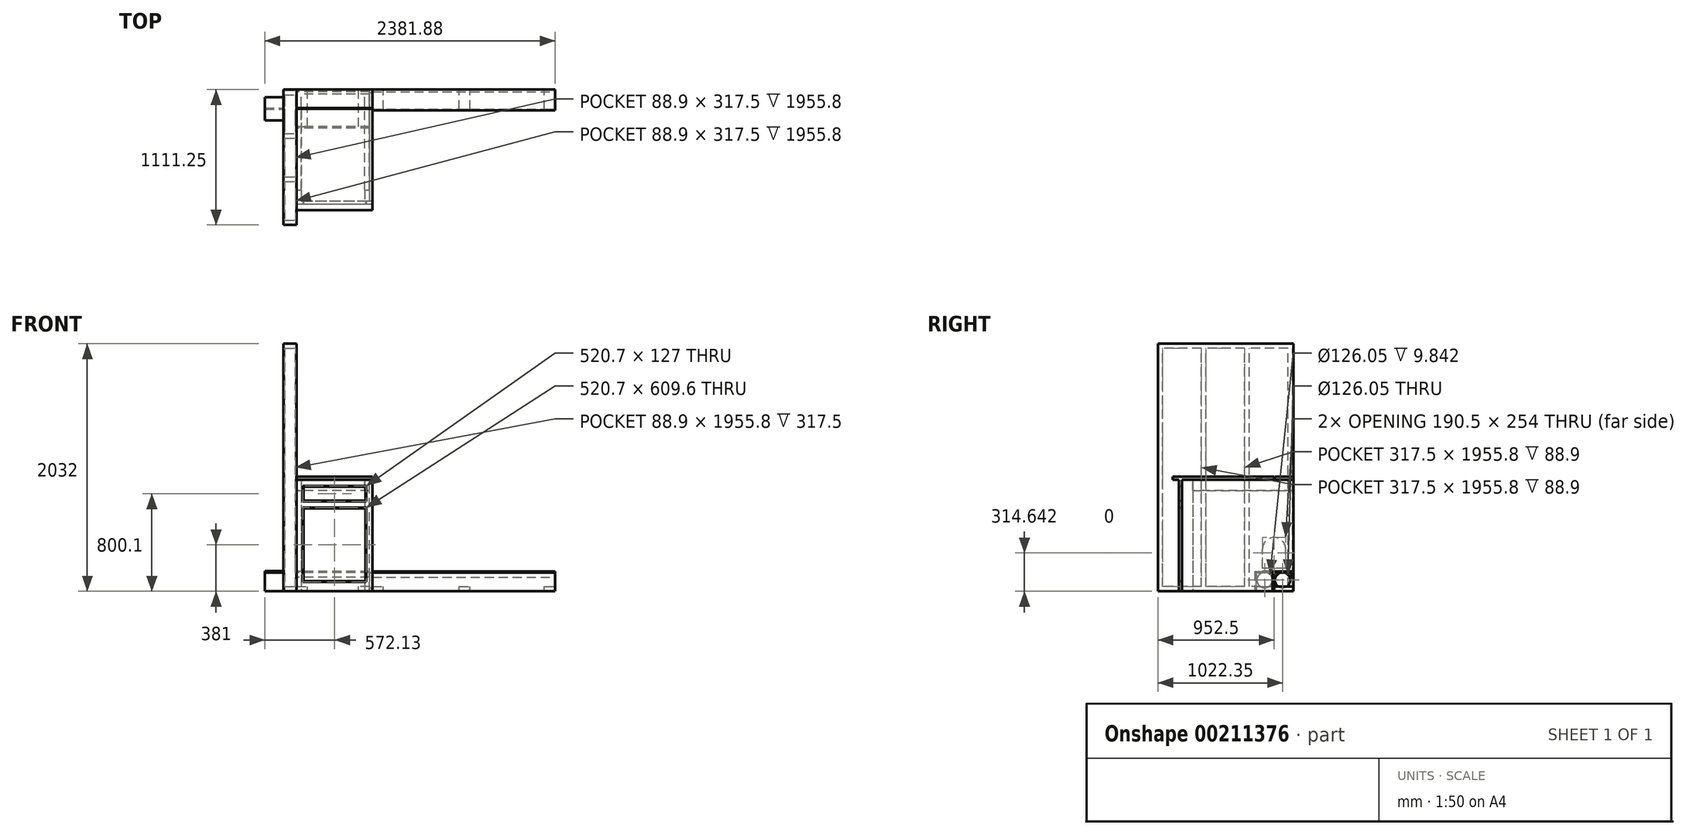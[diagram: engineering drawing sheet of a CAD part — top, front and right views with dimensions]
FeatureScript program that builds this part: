
annotation { "Feature Type Name" : "Feature", "Feature Type Description" : "" }
export const myFeature = defineFeature(function(context is Context, id is Id, definition is map)
    precondition{}
    {
        {
            var Q0;
            Q0=qCreatedBy(makeId("Right.planeOp"),FACE);
            cPlane(context, id + "F0", {"entities" : qUnion([Q0]), "cplaneType" : CPlaneType.OFFSET, "offset" : 1060.45 * mm, "width" : 152.4 * mm, "height" : 152.4 * mm});
        }
        {
            var Q0;
            Q0=qCreatedBy(makeId("Right.planeOp"),FACE);
            cPlane(context, id + "F1", {"entities" : qUnion([Q0]), "cplaneType" : CPlaneType.OFFSET, "offset" : 1060.45 * mm, "oppositeDirection" : true, "width" : 152.4 * mm, "height" : 152.4 * mm});
        }
        {
            var Q0;
            Q0=qCreatedBy(makeId("Top.planeOp"),FACE);
            cPlane(context, id + "F2", {"entities" : qUnion([Q0]), "cplaneType" : CPlaneType.OFFSET, "offset" : 914.4 * mm, "oppositeDirection" : true, "width" : 152.4 * mm, "height" : 152.4 * mm});
        }
        {
            var Q0;
            Q0=qCreatedBy(id+"F2.planeOp",FACE);
            cPlane(context, id + "F3", {"entities" : qUnion([Q0]), "cplaneType" : CPlaneType.OFFSET, "offset" : 2032 * mm, "width" : 152.4 * mm, "height" : 152.4 * mm});
        }
        {
            var Q0;
            Q0=qCreatedBy(makeId("Front.planeOp"),FACE);
            cPlane(context, id + "F4", {"entities" : qUnion([Q0]), "cplaneType" : CPlaneType.OFFSET, "offset" : 914.4 * mm, "oppositeDirection" : true, "width" : 152.4 * mm, "height" : 152.4 * mm});
        }
        {
            var Q0;
            Q0=qCreatedBy(id+"F4.planeOp",FACE);
            cPlane(context, id + "F5", {"entities" : qUnion([Q0]), "cplaneType" : CPlaneType.OFFSET, "offset" : 1111.25 * mm, "width" : 152.4 * mm, "height" : 152.4 * mm});
        }
        {
            var Q0;
            Q0=qCreatedBy(id+"F2.planeOp",FACE);
            var sketch = newSketch(context, id + "F6", { "sketchPlane" : qUnion([Q0])});
            skLineSegment(sketch, "E0.bottom", {"start": v(-1060.45, 914.4) * mm, "end": v(1060.45, 914.4) * mm});
            skLineSegment(sketch, "E0.top", {"start": v(-1060.45, -196.85) * mm, "end": v(1060.45, -196.85) * mm});
            skLineSegment(sketch, "E0.left", {"start": v(-1060.45, 914.4) * mm, "end": v(-1060.45, -196.85) * mm});
            skLineSegment(sketch, "E0.right", {"start": v(1060.45, 914.4) * mm, "end": v(1060.45, -196.85) * mm});
            skSolve(sketch);
        }
        {
            var Q0;
            Q0=qCreatedBy(id+"F2.planeOp",FACE);
            var sketch = newSketch(context, id + "F7", { "sketchPlane" : qUnion([Q0])});
            skLineSegment(sketch, "E1", {"start": v(-1060.45, 0) * mm, "end": v(1060.45, 0) * mm, "construction": true});
            skSolve(sketch);
        }
        {
            var Q0;
            Q0=qCreatedBy(id+"F2.planeOp",FACE);
            var sketch = newSketch(context, id + "F8", { "sketchPlane" : qUnion([Q0])});
            skLineSegment(sketch, "E2", {"start": v(-450.85, 914.4) * mm, "end": v(-450.85, 0) * mm, "construction": true});
            skSolve(sketch);
        }
        {
            var Q0;
            Q0 = qBodyType(qCreatedBy(id + "F8" ,EDGE), BodyType.WIRE);
            var Q1;
            Q1=qCreatedBy(id+"F1.planeOp",FACE);
            cPlane(context, id + "F9", {"entities" : qUnion([Q0, Q1]), "cplaneType" : CPlaneType.LINE_ANGLE, "offset" : 25.4 * mm, "angle" : 0 * degree, "width" : 152.4 * mm, "height" : 152.4 * mm});
        }
        {
            var Q0;
            Q0=qCreatedBy(id+"F2.planeOp",FACE);
            var sketch = newSketch(context, id + "F10", { "sketchPlane" : qUnion([Q0])});
            skPoint(sketch, "E3", {"position": v(1060.45, 825.5) * mm});
            skPoint(sketch, "E4", {"position": v(-1060.45, 679.45) * mm});
            skPoint(sketch, "E5", {"position": v(-1060.45, 342.9) * mm});
            skSolve(sketch);
        }
        {
            var Q0;
            Q0=qCreatedBy(id+"F1.planeOp",FACE);
            var sketch = newSketch(context, id + "F11", { "sketchPlane" : qUnion([Q0])});
            skCircle(sketch, "E6", {"center": v(678.37, -822.33) * mm, "radius": 53.18 * mm});
            skSolve(sketch);
        }
        {
            var Q0;
            Q0=qCreatedBy(id+"F0.planeOp",FACE);
            var sketch = newSketch(context, id + "F12", { "sketchPlane" : qUnion([Q0])});
            skCircle(sketch, "E7", {"center": v(825.5, -822.33) * mm, "radius": 53.18 * mm});
            skSolve(sketch);
        }
        {
            var Q0;
            Q0=makeQuery(id+"F6.imprint","IMPRINT",FACE,{"disambiguationData":[TD([[makeQuery(id+"F6.imprint","IMPRINT",EDGE,{"derivedFrom":sQuery(id+"F6.wireOp",EDGE,"E0.bottom")}),-1.0]])]});
            cPlane(context, id + "F13", {"entities" : qUnion([Q0]), "cplaneType" : CPlaneType.OFFSET, "offset" : 92.07 * mm, "width" : 152.4 * mm, "height" : 152.4 * mm});
        }
        {
            var Q0;
            Q0=qCreatedBy(id+"F13.planeOp",FACE);
            var sketch = newSketch(context, id + "F14", { "sketchPlane" : qUnion([Q0])});
            skLineSegment(sketch, "E8", {"start": v(-1060.45, 678.37) * mm, "end": v(-908.05, 678.37) * mm});
            skLineSegment(sketch, "E9", {"start": v(-908.05, 678.37) * mm, "end": v(-760.92, 825.5) * mm});
            skLineSegment(sketch, "E10", {"start": v(-760.92, 825.5) * mm, "end": v(1060.45, 825.5) * mm});
            skSolve(sketch);
        }
        {
            var Q0;
            Q0 = qSketchRegion(id + "F12", true);
            var Q1;
            Q1=sQuery(id+"F11.wireOp",EDGE,"E6");
            var Q2;
            Q2 = qConstructionFilter(qBodyType(qCreatedBy(id + "F14" ,EDGE), BodyType.WIRE), ConstructionObject.NO);
            sweep(context, id + "F15", {"bodyType" : ToolBodyType.SURFACE, "profiles" : qUnion([Q0]), "surfaceProfiles" : qUnion([Q1]), "path" : qUnion([Q2])});
        }
        {
            var Q0;
            Q0=qCreatedBy(id+"F2.planeOp",FACE);
            var sketch = newSketch(context, id + "F16", { "sketchPlane" : qUnion([Q0])});
            skLineSegment(sketch, "E11", {"start": v(-1060.45, 596.9) * mm, "end": v(1060.45, 596.9) * mm, "construction": true});
            skSolve(sketch);
        }
        {
            var Q0;
            Q0=makeQuery(id+"F6.imprint","IMPRINT",FACE,{"disambiguationData":[TD([[makeQuery(id+"F6.imprint","IMPRINT",EDGE,{"derivedFrom":sQuery(id+"F6.wireOp",EDGE,"E0.bottom")}),-1.0]])]});
            var sketch = newSketch(context, id + "F17", { "sketchPlane" : qUnion([Q0])});
            skPoint(sketch, "E12", {"position": v(1060.45, 742.95) * mm});
            skLineSegment(sketch, "E13", {"start": v(1060.45, 742.95) * mm, "end": v(-1060.45, 742.95) * mm, "construction": true});
            skSolve(sketch);
        }
        {
            var Q0;
            Q0=qCreatedBy(id+"F1.planeOp",FACE);
            var sketch = newSketch(context, id + "F18", { "sketchPlane" : qUnion([Q0])});
            skLineSegment(sketch, "E14.bottom", {"start": v(914.4, -762) * mm, "end": v(596.9, -762) * mm});
            skLineSegment(sketch, "E14.top", {"start": v(914.4, -752.16) * mm, "end": v(596.9, -752.16) * mm});
            skLineSegment(sketch, "E14.left", {"start": v(914.4, -762) * mm, "end": v(914.4, -752.16) * mm});
            skLineSegment(sketch, "E14.right", {"start": v(596.9, -762) * mm, "end": v(596.9, -752.16) * mm});
            skPoint(sketch, "E15.0", {"position": v(914.4, -914.4) * mm});
            skPoint(sketch, "E16.0", {"position": v(596.9, -914.4) * mm});
            skSolve(sketch);
        }
        {
            var Q0;
            Q0=qCreatedBy(id+"F0.planeOp",FACE);
            var sketch = newSketch(context, id + "F19", { "sketchPlane" : qUnion([Q0])});
            skLineSegment(sketch, "E17.bottom", {"start": v(914.4, -752.16) * mm, "end": v(742.95, -752.16) * mm});
            skLineSegment(sketch, "E17.top", {"start": v(914.4, -762) * mm, "end": v(742.95, -762) * mm});
            skLineSegment(sketch, "E17.left", {"start": v(914.4, -752.16) * mm, "end": v(914.4, -762) * mm});
            skLineSegment(sketch, "E17.right", {"start": v(742.95, -752.16) * mm, "end": v(742.95, -762) * mm});
            skSolve(sketch);
        }
        {
            var Q0;
            Q0=qCreatedBy(id+"F9.planeOp",FACE);
            var sketch = newSketch(context, id + "F20", { "sketchPlane" : qUnion([Q0])});
            skLineSegment(sketch, "E18.bottom", {"start": v(-914.4, -914.4) * mm, "end": v(0, -914.4) * mm});
            skLineSegment(sketch, "E18.top", {"start": v(-914.4, 0) * mm, "end": v(0, 0) * mm});
            skLineSegment(sketch, "E18.left", {"start": v(-914.4, -914.4) * mm, "end": v(-914.4, 0) * mm});
            skLineSegment(sketch, "E18.right", {"start": v(0, -914.4) * mm, "end": v(0, 0) * mm});
            skCircle(sketch, "E19", {"center": v(-825.5, -822.33) * mm, "radius": 63.02 * mm});
            skSolve(sketch);
        }
        {
            var Q0;
            Q0 = qSketchRegion(id + "F20", true);
            extrude(context, id + "F21", {"entities" : qUnion([Q0]), "endBound" : BoundingType.SYMMETRIC, "depth" : 25.4 * mm});
        }
        {
            var Q0;
            Q0=makeQuery(id+"F18.imprint","IMPRINT",FACE,{"disambiguationData":[TD([[makeQuery(id+"F18.imprint","IMPRINT",EDGE,{"derivedFrom":sQuery(id+"F18.wireOp",EDGE,"E14.bottom")}),-1.0]])]});
            var Q1;
            Q1=makeQuery(id+"F21.opExtrude","CAP_FACE",FACE,{"disambiguationData":[OSD([sQuery(id+"F20.wireOp",EDGE,"E18.bottom"),sQuery(id+"F20.wireOp",EDGE,"E18.top"),sQuery(id+"F20.wireOp",EDGE,"E18.left"),sQuery(id+"F20.wireOp",EDGE,"E18.right"),sQuery(id+"F20.wireOp",EDGE,"E19")])],"isStart":false});
            extrude(context, id + "F22", {"entities" : qUnion([Q0]), "endBound" : BoundingType.UP_TO_SURFACE, "endBoundEntityFace" : qUnion([Q1]), "depth" : 25.4 * mm});
        }
        {
            var Q0;
            Q0=qCreatedBy(id+"F1.planeOp",FACE);
            var sketch = newSketch(context, id + "F23", { "sketchPlane" : qUnion([Q0])});
            skLineSegment(sketch, "E20.bottom", {"start": v(914.4, -762) * mm, "end": v(895.35, -762) * mm});
            skLineSegment(sketch, "E20.top", {"start": v(914.4, -800.1) * mm, "end": v(895.35, -800.1) * mm});
            skLineSegment(sketch, "E20.left", {"start": v(914.4, -762) * mm, "end": v(914.4, -800.1) * mm});
            skLineSegment(sketch, "E20.right", {"start": v(895.35, -762) * mm, "end": v(895.35, -800.1) * mm});
            skSolve(sketch);
        }
        {
            var Q0;
            Q0 = qSketchRegion(id + "F23", true);
            var Q1;
            Q1=makeQuery(id+"F21.opExtrude","CAP_FACE",FACE,{"disambiguationData":[OSD([sQuery(id+"F20.wireOp",EDGE,"E18.bottom"),sQuery(id+"F20.wireOp",EDGE,"E18.top"),sQuery(id+"F20.wireOp",EDGE,"E18.left"),sQuery(id+"F20.wireOp",EDGE,"E18.right"),sQuery(id+"F20.wireOp",EDGE,"E19")])],"isStart":false});
            extrude(context, id + "F24", {"entities" : qUnion([Q0]), "endBound" : BoundingType.UP_TO_SURFACE, "endBoundEntityFace" : qUnion([Q1]), "depth" : 25.4 * mm});
        }
        {
            var Q0;
            Q0=makeQuery(id+"F19.imprint","IMPRINT",FACE,{"disambiguationData":[TD([[makeQuery(id+"F19.imprint","IMPRINT",EDGE,{"derivedFrom":sQuery(id+"F19.wireOp",EDGE,"E17.bottom")}),1.0]])]});
            var Q1;
            Q1=makeQuery(id+"F21.opExtrude","CAP_FACE",FACE,{"disambiguationData":[OSD([sQuery(id+"F20.wireOp",EDGE,"E18.bottom"),sQuery(id+"F20.wireOp",EDGE,"E18.top"),sQuery(id+"F20.wireOp",EDGE,"E18.left"),sQuery(id+"F20.wireOp",EDGE,"E18.right"),sQuery(id+"F20.wireOp",EDGE,"E19")])],"isStart":true});
            var Q2;
            Q2=makeQuery(id+"F21.opExtrude","SWEPT_BODY",BODY,{"disambiguationData":[OSD([sQuery(id+"F20.wireOp",EDGE,"E18.bottom"),sQuery(id+"F20.wireOp",EDGE,"E18.top"),sQuery(id+"F20.wireOp",EDGE,"E18.left"),sQuery(id+"F20.wireOp",EDGE,"E18.right"),sQuery(id+"F20.wireOp",EDGE,"E19")])]});
            extrude(context, id + "F25", {"entities" : qUnion([Q0]), "endBound" : BoundingType.UP_TO_SURFACE, "oppositeDirection" : true, "endBoundEntityFace" : qUnion([Q1]), "endBoundEntityBody" : qUnion([Q2]), "depth" : 25.4 * mm});
        }
        {
            var Q0;
            Q0=qCreatedBy(id+"F0.planeOp",FACE);
            var sketch = newSketch(context, id + "F26", { "sketchPlane" : qUnion([Q0])});
            skLineSegment(sketch, "E21.bottom", {"start": v(914.4, -762) * mm, "end": v(895.35, -762) * mm});
            skLineSegment(sketch, "E21.top", {"start": v(914.4, -800.1) * mm, "end": v(895.35, -800.1) * mm});
            skLineSegment(sketch, "E21.left", {"start": v(914.4, -762) * mm, "end": v(914.4, -800.1) * mm});
            skLineSegment(sketch, "E21.right", {"start": v(895.35, -762) * mm, "end": v(895.35, -800.1) * mm});
            skSolve(sketch);
        }
        {
            var Q0;
            Q0 = qSketchRegion(id + "F26", true);
            var Q1;
            Q1=makeQuery(id+"F37.boolean.opBoolean","MERGE",FACE,{"derivedFrom":[makeQuery(id+"F21.opExtrude","CAP_FACE",FACE,{"disambiguationData":[OSD([sQuery(id+"F20.wireOp",EDGE,"E18.bottom"),sQuery(id+"F20.wireOp",EDGE,"E18.top"),sQuery(id+"F20.wireOp",EDGE,"E18.left"),sQuery(id+"F20.wireOp",EDGE,"E18.right"),sQuery(id+"F20.wireOp",EDGE,"E19")])],"isStart":true}),makeQuery(id+"F37.opExtrude","SWEPT_FACE",FACE,{"disambiguationData":[OSD([sQuery(id+"F28.wireOp",EDGE,"E22.right")])]})]});
            extrude(context, id + "F27", {"entities" : qUnion([Q0]), "endBound" : BoundingType.UP_TO_SURFACE, "oppositeDirection" : true, "endBoundEntityFace" : qUnion([Q1]), "depth" : 25.4 * mm});
        }
        {
            var Q0;
            Q0=qCreatedBy(makeId("Front.planeOp"),FACE);
            var sketch = newSketch(context, id + "F28", { "sketchPlane" : qUnion([Q0])});
            skLineSegment(sketch, "E22.bottom", {"start": v(-1060.45, -914.4) * mm, "end": v(-438.15, -914.4) * mm});
            skLineSegment(sketch, "E22.top", {"start": v(-1060.45, 0) * mm, "end": v(-438.15, 0) * mm});
            skLineSegment(sketch, "E22.left", {"start": v(-1060.45, -914.4) * mm, "end": v(-1060.45, 0) * mm});
            skLineSegment(sketch, "E22.right", {"start": v(-438.15, -914.4) * mm, "end": v(-438.15, 0) * mm});
            skSolve(sketch);
        }
        {
            var Q0;
            Q0=qCreatedBy(id+"F1.planeOp",FACE);
            var sketch = newSketch(context, id + "F29", { "sketchPlane" : qUnion([Q0])});
            skLineSegment(sketch, "E23.bottom", {"start": v(596.9, -914.4) * mm, "end": v(609.6, -914.4) * mm});
            skLineSegment(sketch, "E23.top", {"start": v(596.9, -762) * mm, "end": v(609.6, -762) * mm});
            skLineSegment(sketch, "E23.left", {"start": v(596.9, -914.4) * mm, "end": v(596.9, -762) * mm});
            skLineSegment(sketch, "E23.right", {"start": v(609.6, -914.4) * mm, "end": v(609.6, -762) * mm});
            skSolve(sketch);
        }
        {
            var Q0;
            Q0 = qSketchRegion(id + "F29", true);
            var Q1;
            Q1=makeQuery(id+"F21.opExtrude","CAP_FACE",FACE,{"disambiguationData":[OSD([sQuery(id+"F20.wireOp",EDGE,"E18.bottom"),sQuery(id+"F20.wireOp",EDGE,"E18.top"),sQuery(id+"F20.wireOp",EDGE,"E18.left"),sQuery(id+"F20.wireOp",EDGE,"E18.right"),sQuery(id+"F20.wireOp",EDGE,"E19")])],"isStart":false});
            extrude(context, id + "F30", {"entities" : qUnion([Q0]), "endBound" : BoundingType.UP_TO_SURFACE, "endBoundEntityFace" : qUnion([Q1]), "depth" : 25.4 * mm});
        }
        {
            var Q0;
            Q0=qCreatedBy(id+"F0.planeOp",FACE);
            var sketch = newSketch(context, id + "F31", { "sketchPlane" : qUnion([Q0])});
            skLineSegment(sketch, "E24.bottom", {"start": v(742.95, -762) * mm, "end": v(752.8, -762) * mm});
            skLineSegment(sketch, "E24.top", {"start": v(742.95, -914.4) * mm, "end": v(752.8, -914.4) * mm});
            skLineSegment(sketch, "E24.left", {"start": v(742.95, -762) * mm, "end": v(742.95, -914.4) * mm});
            skLineSegment(sketch, "E24.right", {"start": v(752.8, -762) * mm, "end": v(752.8, -914.4) * mm});
            skSolve(sketch);
        }
        {
            var Q0;
            Q0 = qSketchRegion(id + "F31", true);
            var Q1;
            Q1=makeQuery(id+"F37.boolean.opBoolean","MERGE",FACE,{"derivedFrom":[makeQuery(id+"F21.opExtrude","CAP_FACE",FACE,{"disambiguationData":[OSD([sQuery(id+"F20.wireOp",EDGE,"E18.bottom"),sQuery(id+"F20.wireOp",EDGE,"E18.top"),sQuery(id+"F20.wireOp",EDGE,"E18.left"),sQuery(id+"F20.wireOp",EDGE,"E18.right"),sQuery(id+"F20.wireOp",EDGE,"E19")])],"isStart":true}),makeQuery(id+"F37.opExtrude","SWEPT_FACE",FACE,{"disambiguationData":[OSD([sQuery(id+"F28.wireOp",EDGE,"E22.right")])]})]});
            extrude(context, id + "F32", {"entities" : qUnion([Q0]), "endBound" : BoundingType.UP_TO_SURFACE, "oppositeDirection" : true, "endBoundEntityFace" : qUnion([Q1]), "depth" : 25.4 * mm});
        }
        {
            var Q0;
            Q0=qCreatedBy(id+"F4.planeOp",FACE);
            var sketch = newSketch(context, id + "F33", { "sketchPlane" : qUnion([Q0])});
            skLineSegment(sketch, "E25.bottom", {"start": v(-1060.45, -914.4) * mm, "end": v(-971.55, -914.4) * mm});
            skLineSegment(sketch, "E25.top", {"start": v(-1060.45, -876.3) * mm, "end": v(-971.55, -876.3) * mm});
            skLineSegment(sketch, "E25.left", {"start": v(-1060.45, -914.4) * mm, "end": v(-1060.45, -876.3) * mm});
            skLineSegment(sketch, "E25.right", {"start": v(-971.55, -914.4) * mm, "end": v(-971.55, -876.3) * mm});
            skLineSegment(sketch, "E26.bottom", {"start": v(-463.55, -914.4) * mm, "end": v(-552.45, -914.4) * mm});
            skLineSegment(sketch, "E26.top", {"start": v(-463.55, -876.3) * mm, "end": v(-552.45, -876.3) * mm});
            skLineSegment(sketch, "E26.left", {"start": v(-463.55, -914.4) * mm, "end": v(-463.55, -876.3) * mm});
            skLineSegment(sketch, "E26.right", {"start": v(-552.45, -914.4) * mm, "end": v(-552.45, -876.3) * mm});
            skSolve(sketch);
        }
        {
            var Q0;
            Q0 = qSketchRegion(id + "F33", true);
            var Q1;
            Q1=makeQuery(id+"F30.opExtrude","SWEPT_FACE",FACE,{"disambiguationData":[OSD([sQuery(id+"F29.wireOp",EDGE,"E23.right")])]});
            extrude(context, id + "F34", {"entities" : qUnion([Q0]), "endBoundEntityFace" : qUnion([Q1]), "depth" : 304.8 * mm});
        }
        {
            var Q0;
            Q0=qCreatedBy(id+"F4.planeOp",FACE);
            var sketch = newSketch(context, id + "F35", { "sketchPlane" : qUnion([Q0])});
            skLineSegment(sketch, "E27.bottom", {"start": v(-438.15, -914.4) * mm, "end": v(-349.25, -914.4) * mm});
            skLineSegment(sketch, "E27.top", {"start": v(-438.15, -876.3) * mm, "end": v(-349.25, -876.3) * mm});
            skLineSegment(sketch, "E27.left", {"start": v(-438.15, -914.4) * mm, "end": v(-438.15, -876.3) * mm});
            skLineSegment(sketch, "E27.right", {"start": v(-349.25, -914.4) * mm, "end": v(-349.25, -876.3) * mm});
            skLineSegment(sketch, "E28.bottom", {"start": v(971.55, -914.4) * mm, "end": v(1060.45, -914.4) * mm});
            skLineSegment(sketch, "E28.top", {"start": v(971.55, -876.3) * mm, "end": v(1060.45, -876.3) * mm});
            skLineSegment(sketch, "E28.left", {"start": v(971.55, -914.4) * mm, "end": v(971.55, -876.3) * mm});
            skLineSegment(sketch, "E28.right", {"start": v(1060.45, -914.4) * mm, "end": v(1060.45, -876.3) * mm});
            skLineSegment(sketch, "E29.bottom", {"start": v(273.05, -914.4) * mm, "end": v(361.95, -914.4) * mm});
            skLineSegment(sketch, "E29.top", {"start": v(273.05, -876.3) * mm, "end": v(361.95, -876.3) * mm});
            skLineSegment(sketch, "E29.left", {"start": v(273.05, -914.4) * mm, "end": v(273.05, -876.3) * mm});
            skLineSegment(sketch, "E29.right", {"start": v(361.95, -914.4) * mm, "end": v(361.95, -876.3) * mm});
            skSolve(sketch);
        }
        {
            var Q0;
            Q0 = qSketchRegion(id + "F35", true);
            var Q1;
            Q1=makeQuery(id+"F32.opExtrude","SWEPT_FACE",FACE,{"disambiguationData":[OSD([sQuery(id+"F31.wireOp",EDGE,"E24.right")])]});
            extrude(context, id + "F36", {"entities" : qUnion([Q0]), "endBound" : BoundingType.UP_TO_SURFACE, "endBoundEntityFace" : qUnion([Q1]), "depth" : 152.4 * mm});
        }
        {
            var Q0;
            Q0 = qSketchRegion(id + "F28", true);
            extrude(context, id + "F37", {"entities" : qUnion([Q0]), "depth" : 25.4 * mm});
        }
        {
            var Q0;
            Q0=makeQuery(id+"F6.imprint","IMPRINT",FACE,{"disambiguationData":[TD([[makeQuery(id+"F6.imprint","IMPRINT",EDGE,{"derivedFrom":sQuery(id+"F6.wireOp",EDGE,"E0.bottom")}),-1.0]])]});
            var sketch = newSketch(context, id + "F38", { "sketchPlane" : qUnion([Q0])});
            skLineSegment(sketch, "E30.bottom", {"start": v(-1060.45, 88.9) * mm, "end": v(-1022.35, 88.9) * mm});
            skLineSegment(sketch, "E30.top", {"start": v(-1060.45, 0) * mm, "end": v(-1022.35, 0) * mm});
            skLineSegment(sketch, "E30.left", {"start": v(-1060.45, 88.9) * mm, "end": v(-1060.45, 0) * mm});
            skLineSegment(sketch, "E30.right", {"start": v(-1022.35, 88.9) * mm, "end": v(-1022.35, 0) * mm});
            skLineSegment(sketch, "E31.bottom", {"start": v(-501.65, 88.9) * mm, "end": v(-463.55, 88.9) * mm});
            skLineSegment(sketch, "E31.top", {"start": v(-501.65, 0) * mm, "end": v(-463.55, 0) * mm});
            skLineSegment(sketch, "E31.left", {"start": v(-501.65, 88.9) * mm, "end": v(-501.65, 0) * mm});
            skLineSegment(sketch, "E31.right", {"start": v(-463.55, 88.9) * mm, "end": v(-463.55, 0) * mm});
            skSolve(sketch);
        }
        {
            var Q0;
            Q0 = qSketchRegion(id + "F38", true);
            var Q1;
            Q1=makeQuery(id+"F37.boolean.opBoolean","MERGE",FACE,{"derivedFrom":[makeQuery(id+"F21.opExtrude","SWEPT_FACE",FACE,{"disambiguationData":[OSD([sQuery(id+"F20.wireOp",EDGE,"E18.top")])]}),makeQuery(id+"F37.opExtrude","SWEPT_FACE",FACE,{"disambiguationData":[OSD([sQuery(id+"F28.wireOp",EDGE,"E22.top")])]})]});
            extrude(context, id + "F39", {"entities" : qUnion([Q0]), "endBound" : BoundingType.UP_TO_SURFACE, "endBoundEntityFace" : qUnion([Q1]), "depth" : 914.4 * mm});
        }
        {
            var Q0;
            Q0=qCreatedBy(id+"F1.planeOp",FACE);
            var sketch = newSketch(context, id + "F40", { "sketchPlane" : qUnion([Q0])});
            skLineSegment(sketch, "E32.bottom", {"start": v(914.4, 0) * mm, "end": v(876.3, 0) * mm});
            skLineSegment(sketch, "E32.top", {"start": v(914.4, -88.9) * mm, "end": v(876.3, -88.9) * mm});
            skLineSegment(sketch, "E32.left", {"start": v(914.4, 0) * mm, "end": v(914.4, -88.9) * mm});
            skLineSegment(sketch, "E32.right", {"start": v(876.3, 0) * mm, "end": v(876.3, -88.9) * mm});
            skSolve(sketch);
        }
        {
            var Q0;
            Q0 = qSketchRegion(id + "F40", true);
            var Q1;
            Q1=makeQuery(id+"F21.opExtrude","CAP_FACE",FACE,{"disambiguationData":[OSD([sQuery(id+"F20.wireOp",EDGE,"E18.bottom"),sQuery(id+"F20.wireOp",EDGE,"E18.top"),sQuery(id+"F20.wireOp",EDGE,"E18.left"),sQuery(id+"F20.wireOp",EDGE,"E18.right"),sQuery(id+"F20.wireOp",EDGE,"E19")])],"isStart":false});
            extrude(context, id + "F41", {"entities" : qUnion([Q0]), "endBound" : BoundingType.UP_TO_SURFACE, "endBoundEntityFace" : qUnion([Q1]), "depth" : 25.4 * mm});
        }
        {
            var Q0;
            Q0=makeQuery(id+"F41.opExtrude","SWEPT_FACE",FACE,{"disambiguationData":[OSD([sQuery(id+"F40.wireOp",EDGE,"E32.right")])]});
            var sketch = newSketch(context, id + "F42", { "sketchPlane" : qUnion([Q0])});
            skLineSegment(sketch, "E33.bottom", {"start": v(-463.55, 0) * mm, "end": v(-501.65, 0) * mm});
            skLineSegment(sketch, "E33.top", {"start": v(-463.55, -88.9) * mm, "end": v(-501.65, -88.9) * mm});
            skLineSegment(sketch, "E33.left", {"start": v(-463.55, 0) * mm, "end": v(-463.55, -88.9) * mm});
            skLineSegment(sketch, "E33.right", {"start": v(-501.65, 0) * mm, "end": v(-501.65, -88.9) * mm});
            skLineSegment(sketch, "E34.bottom", {"start": v(-1060.45, 0) * mm, "end": v(-1022.35, 0) * mm});
            skLineSegment(sketch, "E34.top", {"start": v(-1060.45, -88.9) * mm, "end": v(-1022.35, -88.9) * mm});
            skLineSegment(sketch, "E34.left", {"start": v(-1060.45, 0) * mm, "end": v(-1060.45, -88.9) * mm});
            skLineSegment(sketch, "E34.right", {"start": v(-1022.35, 0) * mm, "end": v(-1022.35, -88.9) * mm});
            skSolve(sketch);
        }
        {
            var Q0;
            Q0 = qSketchRegion(id + "F42", true);
            var Q1;
            Q1=makeQuery(id+"F39.opExtrude","SWEPT_FACE",FACE,{"disambiguationData":[OSD([sQuery(id+"F38.wireOp",EDGE,"E31.bottom")])]});
            var Q2;
            Q2=makeQuery(id+"F41.opExtrude","SWEPT_FACE",FACE,{"disambiguationData":[OSD([sQuery(id+"F40.wireOp",EDGE,"E32.right")])]});
            extrude(context, id + "F43", {"entities" : qUnion([Q0]), "endBound" : BoundingType.UP_TO_SURFACE, "endBoundEntityFace" : qUnion([Q1]), "depth" : 25.4 * mm});
        }
        {
            var Q0;
            Q0=qCreatedBy(makeId("Top.planeOp"),FACE);
            var sketch = newSketch(context, id + "F44", { "sketchPlane" : qUnion([Q0])});
            skLineSegment(sketch, "E35.bottom", {"start": v(-1060.45, 914.4) * mm, "end": v(-438.15, 914.4) * mm});
            skLineSegment(sketch, "E35.top", {"start": v(-1060.45, -76.2) * mm, "end": v(-438.15, -76.2) * mm});
            skLineSegment(sketch, "E35.left", {"start": v(-1060.45, 914.4) * mm, "end": v(-1060.45, 762) * mm});
            skLineSegment(sketch, "E35.right", {"start": v(-438.15, 914.4) * mm, "end": v(-438.15, 762) * mm});
            skLineSegment(sketch, "E36", {"start": v(-1060.45, 762) * mm, "end": v(-438.15, 762) * mm});
            skLineSegment(sketch, "E37", {"start": v(-1060.45, 755.65) * mm, "end": v(-438.15, 755.65) * mm});
            skLineSegment(sketch, "E38.trimOffspring", {"start": v(-438.15, 755.65) * mm, "end": v(-438.15, -76.2) * mm});
            skLineSegment(sketch, "E39.trimOffspring", {"start": v(-1060.45, 755.65) * mm, "end": v(-1060.45, -76.2) * mm});
            skSolve(sketch);
        }
        {
            var Q0;
            Q0 = qSketchRegion(id + "F44", true);
            extrude(context, id + "F45", {"entities" : qUnion([Q0]), "depth" : 25.4 * mm});
        }
        {
            var Q0;
            Q0=makeQuery(id+"F37.opExtrude","CAP_FACE",FACE,{"disambiguationData":[OSD([sQuery(id+"F28.wireOp",EDGE,"E22.bottom"),sQuery(id+"F28.wireOp",EDGE,"E22.top"),sQuery(id+"F28.wireOp",EDGE,"E22.left"),sQuery(id+"F28.wireOp",EDGE,"E22.right")])],"isStart":false});
            var sketch = newSketch(context, id + "F46", { "sketchPlane" : qUnion([Q0])});
            skLineSegment(sketch, "E40.bottom", {"start": v(-1009.65, -228.6) * mm, "end": v(-488.95, -228.6) * mm});
            skLineSegment(sketch, "E40.top", {"start": v(-1009.65, -838.2) * mm, "end": v(-488.95, -838.2) * mm});
            skLineSegment(sketch, "E40.left", {"start": v(-1009.65, -228.6) * mm, "end": v(-1009.65, -838.2) * mm});
            skLineSegment(sketch, "E40.right", {"start": v(-488.95, -228.6) * mm, "end": v(-488.95, -838.2) * mm});
            skLineSegment(sketch, "E41.0", {"start": v(-495.3, -234.95) * mm, "end": v(-495.3, -831.85) * mm});
            skLineSegment(sketch, "E41.1", {"start": v(-1003.3, -234.95) * mm, "end": v(-495.3, -234.95) * mm});
            skLineSegment(sketch, "E41.2", {"start": v(-1003.3, -234.95) * mm, "end": v(-1003.3, -831.85) * mm});
            skLineSegment(sketch, "E41.3", {"start": v(-1003.3, -831.85) * mm, "end": v(-495.3, -831.85) * mm});
            skLineSegment(sketch, "E42.bottom", {"start": v(-1009.65, -50.8) * mm, "end": v(-488.95, -50.8) * mm});
            skLineSegment(sketch, "E42.top", {"start": v(-1009.65, -177.8) * mm, "end": v(-488.95, -177.8) * mm});
            skLineSegment(sketch, "E42.left", {"start": v(-1009.65, -50.8) * mm, "end": v(-1009.65, -177.8) * mm});
            skLineSegment(sketch, "E42.right", {"start": v(-488.95, -50.8) * mm, "end": v(-488.95, -177.8) * mm});
            skLineSegment(sketch, "E43.0", {"start": v(-1003.3, -57.15) * mm, "end": v(-1003.3, -171.45) * mm});
            skLineSegment(sketch, "E43.1", {"start": v(-1003.3, -57.15) * mm, "end": v(-495.3, -57.15) * mm});
            skLineSegment(sketch, "E43.2", {"start": v(-495.3, -57.15) * mm, "end": v(-495.3, -171.45) * mm});
            skLineSegment(sketch, "E43.3", {"start": v(-1003.3, -171.45) * mm, "end": v(-495.3, -171.45) * mm});
            skSolve(sketch);
        }
        {
            var Q0;
            Q0 = qSketchRegion(id + "F46", true);
            extrude(context, id + "F47", {"entities" : qUnion([Q0]), "operationType" : NewBodyOperationType.REMOVE, "oppositeDirection" : true, "depth" : 25.4 * mm});
        }
        {
            var Q0;
            Q0=qCreatedBy(id+"F1.planeOp",FACE);
            var sketch = newSketch(context, id + "F48", { "sketchPlane" : qUnion([Q0])});
            skLineSegment(sketch, "E44.bottom", {"start": v(914.4, 1117.6) * mm, "end": v(-196.85, 1117.6) * mm});
            skLineSegment(sketch, "E44.top", {"start": v(914.4, -914.4) * mm, "end": v(-196.85, -914.4) * mm});
            skLineSegment(sketch, "E44.left", {"start": v(914.4, 1117.6) * mm, "end": v(914.4, -914.4) * mm});
            skLineSegment(sketch, "E44.right", {"start": v(-196.85, 1117.6) * mm, "end": v(-196.85, -914.4) * mm});
            skCircle(sketch, "E45", {"center": v(678.37, -822.33) * mm, "radius": 63.02 * mm});
            skLineSegment(sketch, "E46.bottom", {"start": v(850.9, -726.76) * mm, "end": v(660.4, -726.76) * mm});
            skLineSegment(sketch, "E46.left", {"start": v(850.9, -726.76) * mm, "end": v(850.9, -568) * mm});
            skLineSegment(sketch, "E46.right", {"start": v(660.4, -726.76) * mm, "end": v(660.4, -568) * mm});
            skArc(sketch, "E47", {"start": v(850.9, -568) * mm, "mid": v(755.65, -472.76) * mm, "end": v(660.4, -568) * mm});
            skSolve(sketch);
        }
        {
            var Q0;
            Q0 = qSketchRegion(id + "F48", true);
            extrude(context, id + "F49", {"entities" : qUnion([Q0]), "oppositeDirection" : true, "depth" : 9.84 * mm});
        }
        {
            var Q0;
            Q0=makeQuery(id+"F49.opExtrude","CAP_FACE",FACE,{"disambiguationData":[OSD([sQuery(id+"F48.wireOp",EDGE,"E44.bottom"),sQuery(id+"F48.wireOp",EDGE,"E44.top"),sQuery(id+"F48.wireOp",EDGE,"E44.left"),sQuery(id+"F48.wireOp",EDGE,"E44.right"),sQuery(id+"F48.wireOp",EDGE,"E45"),sQuery(id+"F48.wireOp",EDGE,"E46.bottom"),sQuery(id+"F48.wireOp",EDGE,"E46.left"),sQuery(id+"F48.wireOp",EDGE,"E46.right"),sQuery(id+"F48.wireOp",EDGE,"E47")])],"isStart":false});
            var sketch = newSketch(context, id + "F50", { "sketchPlane" : qUnion([Q0])});
            skLineSegment(sketch, "E48.bottom", {"start": v(196.85, -914.4) * mm, "end": v(158.75, -914.4) * mm});
            skLineSegment(sketch, "E48.top", {"start": v(196.85, 1117.6) * mm, "end": v(158.75, 1117.6) * mm});
            skLineSegment(sketch, "E48.left", {"start": v(196.85, -914.4) * mm, "end": v(196.85, 1117.6) * mm});
            skLineSegment(sketch, "E48.right", {"start": v(158.75, -876.3) * mm, "end": v(158.75, 1079.5) * mm});
            skLineSegment(sketch, "E49", {"start": v(177.8, 1117.6) * mm, "end": v(177.8, -914.4) * mm, "construction": true});
            skLineSegment(sketch, "E50.1.0.0", {"start": v(-196.85, -876.3) * mm, "end": v(-196.85, 1079.5) * mm});
            skLineSegment(sketch, "E50.1.0.1", {"start": v(-158.75, -876.3) * mm, "end": v(-158.75, 1079.5) * mm});
            skLineSegment(sketch, "E50.1.0.2", {"start": v(-177.8, 1117.6) * mm, "end": v(-177.8, -914.4) * mm, "construction": true});
            skLineSegment(sketch, "E50.1.0.3", {"start": v(-158.75, -914.4) * mm, "end": v(-196.85, -914.4) * mm});
            skLineSegment(sketch, "E50.1.0.4", {"start": v(-158.75, 1117.6) * mm, "end": v(-196.85, 1117.6) * mm});
            skLineSegment(sketch, "E50.2.0.0", {"start": v(-552.45, -876.3) * mm, "end": v(-552.45, 1079.5) * mm});
            skLineSegment(sketch, "E50.2.0.1", {"start": v(-514.35, -876.3) * mm, "end": v(-514.35, 1079.5) * mm});
            skLineSegment(sketch, "E50.2.0.2", {"start": v(-533.4, 1117.6) * mm, "end": v(-533.4, -914.4) * mm, "construction": true});
            skLineSegment(sketch, "E50.2.0.3", {"start": v(-514.35, -914.4) * mm, "end": v(-552.45, -914.4) * mm});
            skLineSegment(sketch, "E50.2.0.4", {"start": v(-514.35, 1117.6) * mm, "end": v(-552.45, 1117.6) * mm});
            skLineSegment(sketch, "E50.3.0.0", {"start": v(-908.05, -914.4) * mm, "end": v(-908.05, 1117.6) * mm});
            skLineSegment(sketch, "E50.3.0.1", {"start": v(-869.95, -876.3) * mm, "end": v(-869.95, 1079.5) * mm});
            skLineSegment(sketch, "E50.3.0.2", {"start": v(-889, 1117.6) * mm, "end": v(-889, -914.4) * mm, "construction": true});
            skLineSegment(sketch, "E50.3.0.3", {"start": v(-869.95, -914.4) * mm, "end": v(-908.05, -914.4) * mm});
            skLineSegment(sketch, "E50.3.0.4", {"start": v(-869.95, 1117.6) * mm, "end": v(-908.05, 1117.6) * mm});
            skLineSegment(sketch, "E50.direction1", {"start": v(158.75, -914.4) * mm, "end": v(-196.85, -914.4) * mm, "construction": true});
            skLineSegment(sketch, "E51.bottom", {"start": v(-908.05, -914.4) * mm, "end": v(196.85, -914.4) * mm});
            skLineSegment(sketch, "E51.top", {"start": v(-908.05, -876.3) * mm, "end": v(196.85, -876.3) * mm});
            skLineSegment(sketch, "E51.left", {"start": v(-908.05, -914.4) * mm, "end": v(-908.05, -876.3) * mm});
            skLineSegment(sketch, "E51.right", {"start": v(196.85, -914.4) * mm, "end": v(196.85, -876.3) * mm});
            skLineSegment(sketch, "E52.bottom", {"start": v(-914.4, 1117.6) * mm, "end": v(196.85, 1117.6) * mm});
            skLineSegment(sketch, "E52.top", {"start": v(-914.4, 1079.5) * mm, "end": v(196.85, 1079.5) * mm});
            skLineSegment(sketch, "E52.left", {"start": v(-914.4, 1117.6) * mm, "end": v(-914.4, 1079.5) * mm});
            skLineSegment(sketch, "E52.right", {"start": v(196.85, 1117.6) * mm, "end": v(196.85, 1079.5) * mm});
            skLineSegment(sketch, "E53", {"start": v(-908.05, 1079.5) * mm, "end": v(-869.95, 1079.5) * mm});
            skLineSegment(sketch, "E54", {"start": v(-552.45, 1079.5) * mm, "end": v(-514.35, 1079.5) * mm});
            skLineSegment(sketch, "E55", {"start": v(-196.85, 1079.5) * mm, "end": v(-158.75, 1079.5) * mm});
            skLineSegment(sketch, "E56", {"start": v(158.75, 1079.5) * mm, "end": v(196.85, 1079.5) * mm});
            skLineSegment(sketch, "E57", {"start": v(-908.05, -876.3) * mm, "end": v(-869.95, -876.3) * mm});
            skLineSegment(sketch, "E58", {"start": v(-552.45, -876.3) * mm, "end": v(-514.35, -876.3) * mm});
            skLineSegment(sketch, "E59", {"start": v(-196.85, -876.3) * mm, "end": v(-158.75, -876.3) * mm});
            skLineSegment(sketch, "E60", {"start": v(158.75, -876.3) * mm, "end": v(196.85, -876.3) * mm});
            skSolve(sketch);
        }
        {
            var Q0;
            Q0 = qSketchRegion(id + "F50", true);
            var Q1;
            Q1=makeQuery(id+"F50.imprint","IMPRINT",FACE,{"disambiguationData":[TD([[makeQuery(id+"F50.imprint","IMPRINT",EDGE,{"derivedFrom":sQuery(id+"F50.wireOp",EDGE,"E50.2.0.0")}),-1.0]])]});
            var Q2;
            Q2=makeQuery(id+"F50.imprint","IMPRINT",FACE,{"disambiguationData":[TD([[makeQuery(id+"F50.imprint","IMPRINT",EDGE,{"derivedFrom":sQuery(id+"F50.wireOp",EDGE,"E50.1.0.0")}),-1.0]])]});
            extrude(context, id + "F51", {"entities" : qUnion([Q0, Q1, Q2]), "depth" : 88.9 * mm});
        }
        {
            var Q0;
            Q0=makeQuery(id+"F51.opExtrude","CAP_FACE",FACE,{"disambiguationData":[OSD([sQuery(id+"F50.wireOp",EDGE,"E48.left"),sQuery(id+"F50.wireOp",EDGE,"E48.right"),sQuery(id+"F50.wireOp",EDGE,"E50.1.0.0"),sQuery(id+"F50.wireOp",EDGE,"E50.1.0.1"),sQuery(id+"F50.wireOp",EDGE,"E50.2.0.0"),sQuery(id+"F50.wireOp",EDGE,"E50.2.0.1"),sQuery(id+"F50.wireOp",EDGE,"E50.3.0.0"),sQuery(id+"F50.wireOp",EDGE,"E50.3.0.1"),sQuery(id+"F50.wireOp",EDGE,"E51.bottom"),sQuery(id+"F50.wireOp",EDGE,"E51.top"),sQuery(id+"F50.wireOp",EDGE,"E51.left"),sQuery(id+"F50.wireOp",EDGE,"E51.right"),sQuery(id+"F50.wireOp",EDGE,"E52.bottom"),sQuery(id+"F50.wireOp",EDGE,"E52.top"),sQuery(id+"F50.wireOp",EDGE,"E52.left"),sQuery(id+"F50.wireOp",EDGE,"E52.right")])],"isStart":false});
            var Q1;
            Q1=makeQuery(id+"F51.opExtrude","CAP_FACE",FACE,{"disambiguationData":[OSD([sQuery(id+"F50.wireOp",EDGE,"E48.left"),sQuery(id+"F50.wireOp",EDGE,"E48.right"),sQuery(id+"F50.wireOp",EDGE,"E50.1.0.0"),sQuery(id+"F50.wireOp",EDGE,"E50.1.0.1"),sQuery(id+"F50.wireOp",EDGE,"E50.2.0.0"),sQuery(id+"F50.wireOp",EDGE,"E50.2.0.1"),sQuery(id+"F50.wireOp",EDGE,"E50.3.0.0"),sQuery(id+"F50.wireOp",EDGE,"E50.3.0.1"),sQuery(id+"F50.wireOp",EDGE,"E51.bottom"),sQuery(id+"F50.wireOp",EDGE,"E51.top"),sQuery(id+"F50.wireOp",EDGE,"E51.left"),sQuery(id+"F50.wireOp",EDGE,"E51.right"),sQuery(id+"F50.wireOp",EDGE,"E52.bottom"),sQuery(id+"F50.wireOp",EDGE,"E52.top"),sQuery(id+"F50.wireOp",EDGE,"E52.left"),sQuery(id+"F50.wireOp",EDGE,"E52.right")])],"isStart":true});
            cPlane(context, id + "F52", {"entities" : qUnion([Q0, Q1]), "cplaneType" : CPlaneType.MID_PLANE, "offset" : 25.4 * mm, "width" : 152.4 * mm, "height" : 152.4 * mm});
        }
        {
            var Q0;
            Q0=makeQuery(id+"F49.opExtrude","SWEPT_BODY",BODY,{"disambiguationData":[OSD([sQuery(id+"F48.wireOp",EDGE,"E44.bottom"),sQuery(id+"F48.wireOp",EDGE,"E44.top"),sQuery(id+"F48.wireOp",EDGE,"E44.left"),sQuery(id+"F48.wireOp",EDGE,"E44.right"),sQuery(id+"F48.wireOp",EDGE,"E45"),sQuery(id+"F48.wireOp",EDGE,"E46.bottom"),sQuery(id+"F48.wireOp",EDGE,"E46.left"),sQuery(id+"F48.wireOp",EDGE,"E46.right"),sQuery(id+"F48.wireOp",EDGE,"E47")])]});
            var Q1;
            Q1=qCreatedBy(id+"F52.planeOp",FACE);
            mirror(context, id + "F53", {"operationType" : NewBodyOperationType.ADD, "entities" : qUnion([Q0]), "mirrorPlane" : qUnion([Q1])});
        }
        {
            var Q0;
            Q0=makeQuery(id+"F53.opPattern","COPY",FACE,{"derivedFrom":makeQuery(id+"F49.opExtrude","CAP_FACE",FACE,{"disambiguationData":[OSD([sQuery(id+"F48.wireOp",EDGE,"E44.bottom"),sQuery(id+"F48.wireOp",EDGE,"E44.top"),sQuery(id+"F48.wireOp",EDGE,"E44.left"),sQuery(id+"F48.wireOp",EDGE,"E44.right"),sQuery(id+"F48.wireOp",EDGE,"E45"),sQuery(id+"F48.wireOp",EDGE,"E46.bottom"),sQuery(id+"F48.wireOp",EDGE,"E46.left"),sQuery(id+"F48.wireOp",EDGE,"E46.right"),sQuery(id+"F48.wireOp",EDGE,"E47")])],"isStart":true}),"instanceName":"1"});
            var sketch = newSketch(context, id + "F54", { "sketchPlane" : qUnion([Q0])});
            skLineSegment(sketch, "E61.bottom", {"start": v(-850.9, -749.47) * mm, "end": v(-660.4, -749.47) * mm});
            skLineSegment(sketch, "E61.top", {"start": v(-850.9, -759.3) * mm, "end": v(-660.4, -759.3) * mm});
            skLineSegment(sketch, "E61.left", {"start": v(-850.9, -749.47) * mm, "end": v(-850.9, -759.3) * mm});
            skLineSegment(sketch, "E61.right", {"start": v(-660.4, -749.47) * mm, "end": v(-660.4, -759.3) * mm});
            skLineSegment(sketch, "E62.bottom", {"start": v(-762, -759.3) * mm, "end": v(-752.16, -759.3) * mm});
            skLineSegment(sketch, "E62.top", {"start": v(-762, -914.4) * mm, "end": v(-752.16, -914.4) * mm});
            skLineSegment(sketch, "E62.left", {"start": v(-762, -759.3) * mm, "end": v(-762, -914.4) * mm});
            skLineSegment(sketch, "E62.right", {"start": v(-752.16, -759.3) * mm, "end": v(-752.16, -914.4) * mm});
            skSolve(sketch);
        }
        {
            var Q0;
            Q0 = qSketchRegion(id + "F54", true);
            extrude(context, id + "F55", {"entities" : qUnion([Q0]), "depth" : 152.4 * mm});
        }
    });
